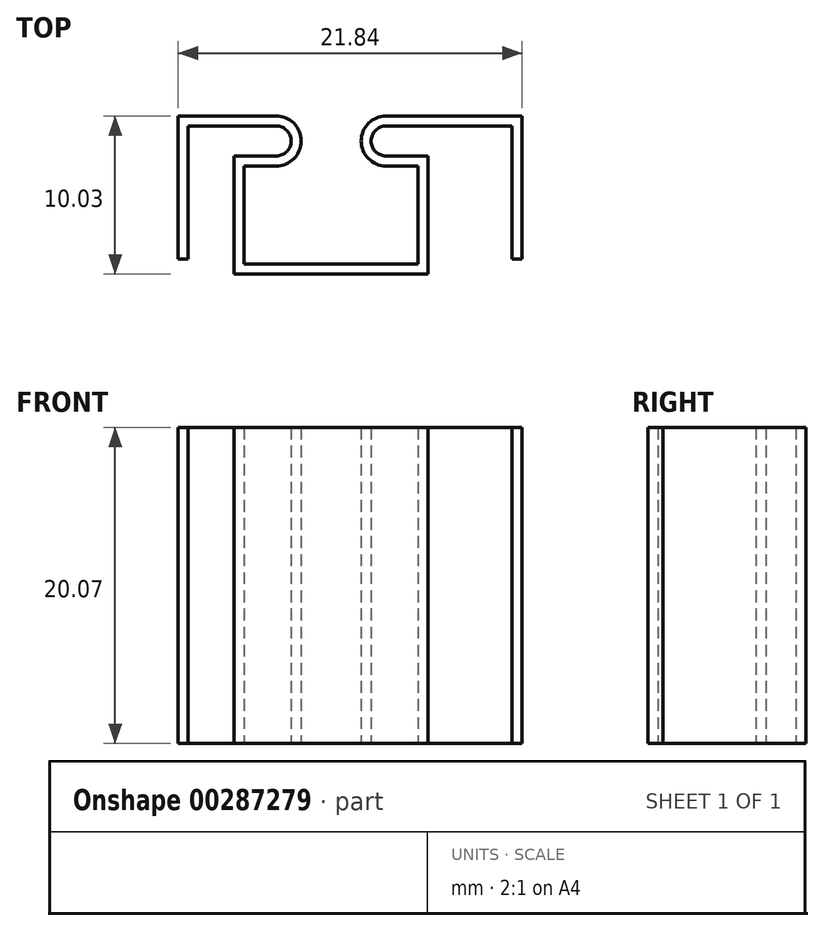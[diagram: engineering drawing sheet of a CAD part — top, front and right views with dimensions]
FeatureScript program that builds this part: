
annotation { "Feature Type Name" : "Feature", "Feature Type Description" : "" }
export const myFeature = defineFeature(function(context is Context, id is Id, definition is map)
    precondition{}
    {
        {
            var Q0;
            Q0=qCreatedBy(makeId("Top.planeOp"),FACE);
            var sketch = newSketch(context, id + "F0", { "sketchPlane" : qUnion([Q0])});
            skLineSegment(sketch, "E0", {"start": v(0, 0) * mm, "end": v(0, 9.1) * mm});
            skLineSegment(sketch, "E1", {"start": v(0, 9.1) * mm, "end": v(6.22, 9.1) * mm});
            skLineSegment(sketch, "E2", {"start": v(4.2, 5.92) * mm, "end": v(4.2, -0.3) * mm});
            skLineSegment(sketch, "E3", {"start": v(4.2, -0.3) * mm, "end": v(15.24, -0.3) * mm});
            skArc(sketch, "E4", {"start": v(6.22, 5.92) * mm, "mid": v(7.81, 7.5) * mm, "end": v(6.22, 9.1) * mm});
            skLineSegment(sketch, "E5", {"start": v(6.22, 5.92) * mm, "end": v(4.2, 5.92) * mm});
            skLineSegment(sketch, "E6.MirrorCS", {"start": v(15.24, 5.92) * mm, "end": v(15.24, -0.3) * mm});
            skLineSegment(sketch, "E7.MirrorCS", {"start": v(13.2, 5.92) * mm, "end": v(15.24, 5.92) * mm});
            skArc(sketch, "E8.MirrorCS", {"start": v(13.2, 5.92) * mm, "mid": v(11.62, 7.5) * mm, "end": v(13.2, 9.1) * mm});
            skLineSegment(sketch, "E9.MirrorCS", {"start": v(21.84, 9.1) * mm, "end": v(13.2, 9.1) * mm});
            skLineSegment(sketch, "E10.MirrorCS", {"start": v(21.84, 0) * mm, "end": v(21.84, 9.1) * mm});
            skLineSegment(sketch, "E11.0", {"start": v(21.2, 0) * mm, "end": v(21.2, 8.46) * mm});
            skArc(sketch, "E11.3", {"start": v(13.2, 6.55) * mm, "mid": v(12.26, 7.5) * mm, "end": v(13.2, 8.46) * mm});
            skArc(sketch, "E11.4", {"start": v(6.22, 6.55) * mm, "mid": v(7.18, 7.5) * mm, "end": v(6.22, 8.46) * mm});
            skLineSegment(sketch, "E11.6", {"start": v(0.63, 8.46) * mm, "end": v(6.22, 8.46) * mm});
            skLineSegment(sketch, "E11.7", {"start": v(0.63, 0) * mm, "end": v(0.63, 8.46) * mm});
            skLineSegment(sketch, "E11.8", {"start": v(6.22, 6.55) * mm, "end": v(3.56, 6.55) * mm});
            skLineSegment(sketch, "E11.9", {"start": v(3.56, 6.55) * mm, "end": v(3.56, -0.94) * mm});
            skLineSegment(sketch, "E11.10", {"start": v(3.56, -0.94) * mm, "end": v(15.88, -0.94) * mm});
            skLineSegment(sketch, "E11.12", {"start": v(15.88, 6.55) * mm, "end": v(15.88, -0.94) * mm});
            skLineSegment(sketch, "E11.13", {"start": v(13.2, 6.55) * mm, "end": v(15.88, 6.55) * mm});
            skLineSegment(sketch, "E12", {"start": v(0.63, 0) * mm, "end": v(0, 0) * mm});
            skLineSegment(sketch, "E13", {"start": v(21.84, 0) * mm, "end": v(21.2, 0) * mm});
            skLineSegment(sketch, "E14", {"start": v(13.2, 8.46) * mm, "end": v(21.2, 8.46) * mm});
            skSolve(sketch);
        }
        {
            var Q0;
            Q0 = qSketchRegion(id + "F0", true);
            extrude(context, id + "F1", {"entities" : qUnion([Q0]), "depth" : 20.07 * mm});
        }
    });
